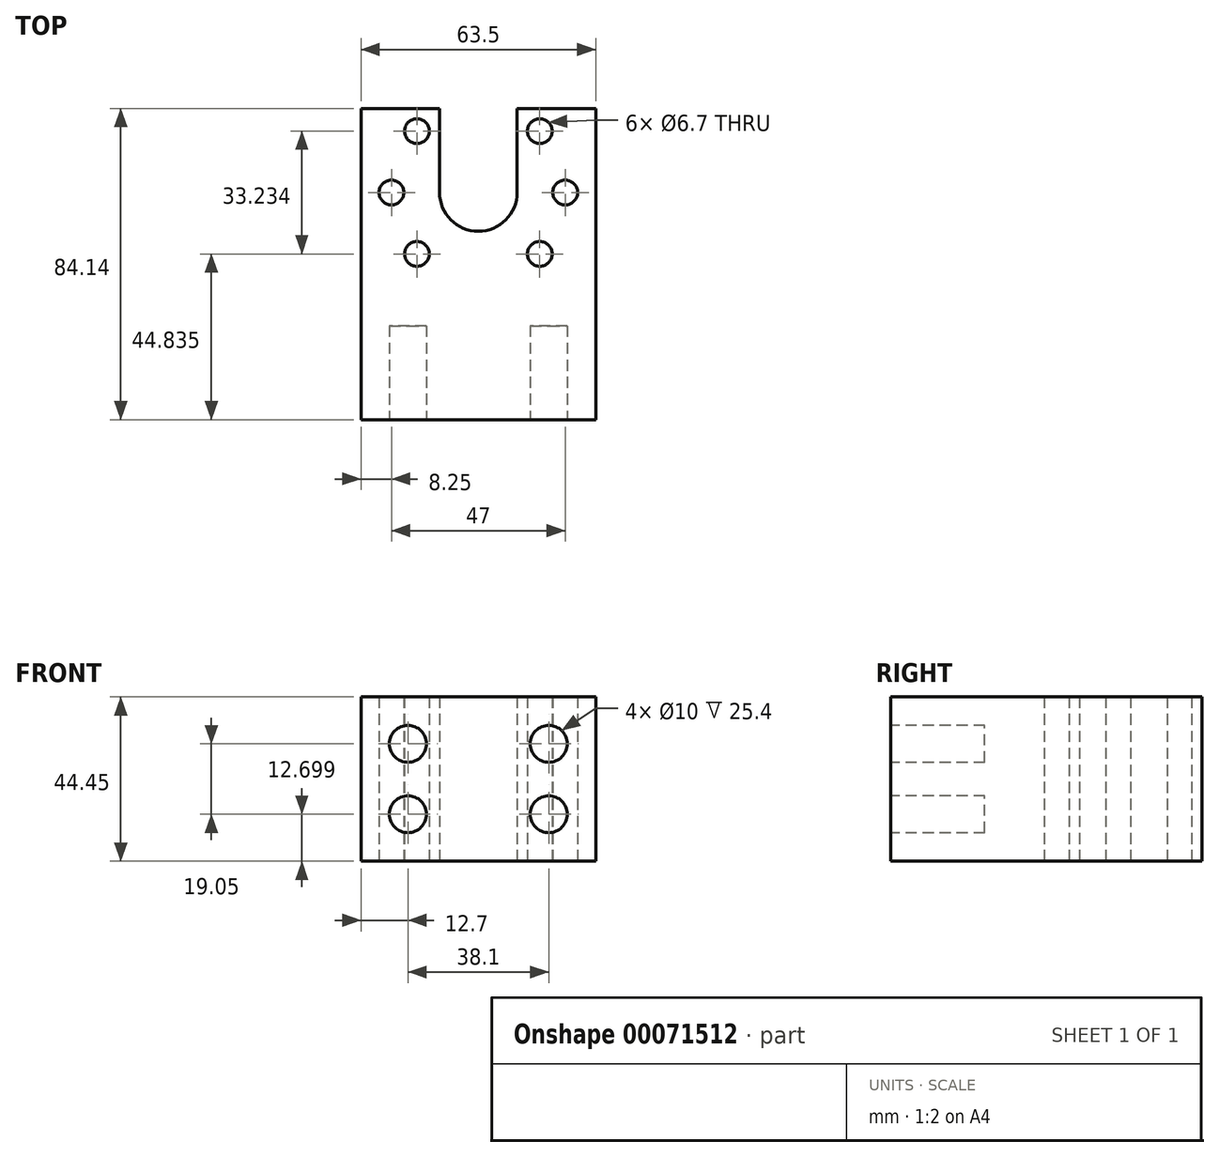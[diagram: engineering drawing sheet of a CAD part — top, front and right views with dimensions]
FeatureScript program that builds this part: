
annotation { "Feature Type Name" : "Feature", "Feature Type Description" : "" }
export const myFeature = defineFeature(function(context is Context, id is Id, definition is map)
    precondition{}
    {
        {
            var Q0;
            Q0=qCreatedBy(makeId("Front.planeOp"),FACE);
            var sketch = newSketch(context, id + "F0", { "sketchPlane" : qUnion([Q0])});
            skLineSegment(sketch, "E0.bottom", {"start": v(-64.99, 25.07) * mm, "end": v(-1.49, 25.07) * mm});
            skLineSegment(sketch, "E0.top", {"start": v(-64.99, -19.38) * mm, "end": v(-1.49, -19.38) * mm});
            skLineSegment(sketch, "E0.left", {"start": v(-64.99, 25.07) * mm, "end": v(-64.99, -19.38) * mm});
            skLineSegment(sketch, "E0.right", {"start": v(-1.49, 25.07) * mm, "end": v(-1.49, -19.38) * mm});
            skSolve(sketch);
        }
        {
            var Q0;
            Q0=qSketchRegion(id+"F0",true);
            extrude(context, id + "F1", {"entities" : qUnion([Q0]), "depth" : 84.14 * mm});
        }
        {
            var Q0;
            Q0=makeQuery(id+"F1.opExtrude","CAP_FACE",FACE,{"disambiguationData":[OSD([sQuery(id+"F0.wireOp",EDGE,"E0.bottom"),sQuery(id+"F0.wireOp",EDGE,"E0.top"),sQuery(id+"F0.wireOp",EDGE,"E0.left"),sQuery(id+"F0.wireOp",EDGE,"E0.right")])],"isStart":false});
            var sketch = newSketch(context, id + "F2", { "sketchPlane" : qUnion([Q0])});
            skCircle(sketch, "E1", {"center": v(-52.29, 12.37) * mm, "radius": 5 * mm});
            skCircle(sketch, "E2.0.1.0", {"center": v(-52.29, -6.68) * mm, "radius": 5 * mm});
            skCircle(sketch, "E2.1.0.0", {"center": v(-14.19, 12.37) * mm, "radius": 5 * mm});
            skCircle(sketch, "E2.1.1.0", {"center": v(-14.19, -6.68) * mm, "radius": 5 * mm});
            skLineSegment(sketch, "E2.direction1", {"start": v(-52.29, 12.37) * mm, "end": v(-14.19, 12.37) * mm, "construction": true});
            skLineSegment(sketch, "E2.direction2", {"start": v(-52.29, 12.37) * mm, "end": v(-52.29, -6.68) * mm, "construction": true});
            skSolve(sketch);
        }
        {
            var Q0;
            Q0=qSketchRegion(id+"F2",true);
            extrude(context, id + "F3", {"entities" : qUnion([Q0]), "operationType" : NewBodyOperationType.REMOVE, "oppositeDirection" : true, "depth" : 25.4 * mm});
        }
        {
            var Q0;
            Q0=makeQuery(id+"F1.opExtrude","SWEPT_FACE",FACE,{"disambiguationData":[OSD([sQuery(id+"F0.wireOp",EDGE,"E0.top")])]});
            var sketch = newSketch(context, id + "F4", { "sketchPlane" : qUnion([Q0])});
            skCircle(sketch, "E3", {"center": v(-56.74, 22.69) * mm, "radius": 3.35 * mm});
            skCircle(sketch, "E4.1.0", {"center": v(-49.86, 6.07) * mm, "radius": 3.35 * mm});
            skCircle(sketch, "E4.3.0", {"center": v(-16.62, 6.07) * mm, "radius": 3.35 * mm});
            skCircle(sketch, "E4.4.0", {"center": v(-9.74, 22.69) * mm, "radius": 3.35 * mm});
            skCircle(sketch, "E4.5.0", {"center": v(-16.62, 39.3) * mm, "radius": 3.35 * mm});
            skCircle(sketch, "E4.7.0", {"center": v(-49.86, 39.3) * mm, "radius": 3.35 * mm});
            skPoint(sketch, "E4.center", {"position": v(-33.24, 22.69) * mm});
            skArc(sketch, "E5", {"start": v(-22.74, 22.69) * mm, "mid": v(-33.24, 33.19) * mm, "end": v(-43.74, 22.69) * mm});
            skLineSegment(sketch, "E6.top", {"start": v(-43.74, 0) * mm, "end": v(-22.74, 0) * mm});
            skLineSegment(sketch, "E6.left", {"start": v(-43.74, 22.69) * mm, "end": v(-43.74, 0) * mm});
            skLineSegment(sketch, "E6.right", {"start": v(-22.74, 22.69) * mm, "end": v(-22.74, 0) * mm});
            skSolve(sketch);
        }
        {
            var Q0;
            Q0=qSketchRegion(id+"F4",true);
            extrude(context, id + "F5", {"entities" : qUnion([Q0]), "operationType" : NewBodyOperationType.REMOVE, "endBound" : BoundingType.THROUGH_ALL, "oppositeDirection" : true, "depth" : 25 * mm});
        }
    });
